FCSTD DOCUMENT  (FreeCAD 2024.1R35694 (Git))
Label: slotting_head_base_plate
License: All rights reserved
LicenseURL: https://en.wikipedia.org/wiki/All_rights_reserved
objects: Assembly::JointGroup×1, App::Part×1, Assembly::AssemblyObject×1, Sketcher::SketchObject×1
note: 1 computed .brp shape members not serialized (recipe doc carries the construction recipe); baked Part::Feature solids carry a one-line shape summary decoded from their .brp

FEATURE [Assembly::JointGroup] Joints
FEATURE [App::Part] Part
  Origin = -> Origin001
FEATURE [Assembly::AssemblyObject] Assembly
  Group = -> [Joints,Part]
  Origin = -> Origin
  Type = Assembly
FEATURE [Sketcher::SketchObject] Sketch
  FullyConstrained = true
  MapMode = 2
  Support = -> [Part]
  sketch-geometry (11):
    g0: LineSegment StartX=-182.5 StartY=135 StartZ=0 EndX=-182.5 EndY=-135 EndZ=0
    g1: LineSegment StartX=-182.5 StartY=-135 StartZ=0 EndX=182.5 EndY=-135 EndZ=0
    g2: LineSegment StartX=182.5 StartY=-135 StartZ=0 EndX=182.5 EndY=135 EndZ=0
    g3: LineSegment StartX=182.5 StartY=135 StartZ=0 EndX=-182.5 EndY=135 EndZ=0
    g4: Circle CenterX=0 CenterY=0 CenterZ=0 NormalX=0 NormalY=0 NormalZ=1 AngleXU=0 Radius=80
    g5: Circle CenterX=125 CenterY=-100 CenterZ=0 NormalX=0 NormalY=0 NormalZ=1 AngleXU=0 Radius=11
    g6: Circle CenterX=-125 CenterY=-100 CenterZ=0 NormalX=0 NormalY=0 NormalZ=1 AngleXU=0 Radius=11
    g7: Circle CenterX=-125 CenterY=100 CenterZ=0 NormalX=0 NormalY=0 NormalZ=1 AngleXU=0 Radius=11
    g8: Circle CenterX=125 CenterY=100 CenterZ=0 NormalX=0 NormalY=0 NormalZ=1 AngleXU=0 Radius=11
    g9: LineSegment StartX=-136 StartY=111 StartZ=0 EndX=136 EndY=111 EndZ=0
    g10: LineSegment StartX=136 StartY=111 StartZ=0 EndX=136 EndY=-111 EndZ=0
  constraints (26):
    c: Coincident(g0,g1)
    c: Coincident(g1,g2)
    c: Coincident(g2,g3)
    c: Coincident(g3,g0)
    c: Vertical(g2)
    c: Horizontal(g1)
    c: DistanceY(g2,g2) = 270  'Pionowy Bok'
    c: DistanceX(g3,g3) = 365  'Poziomy Bok'
    c: Coincident(g4,g-1)
    c: Diameter(g4) = 160
    c: Symmetric(g0,g2,g-2)
    c: Symmetric(g0,g0,g-1)
    c: Radius(g5) = 11
    c: DistanceX(g9,g9) = 272
    c: Symmetric(g9,g9,g-2)
    c: Coincident(g10,g9)
    c: DistanceY(g10,g10) = 222
    c: Symmetric(g9,g10,g-1)
    c: Diameter(g8) = 22
    c: Tangent(g8,g9)
    c: Tangent(g8,g10)
    c: Symmetric(g8,g7,g-2)
    c: Symmetric(g8,g5,g-1)
    c: Symmetric(g5,g6,g-2)
    c: Diameter(g7) = 22
    c: Diameter(g6) = 22
